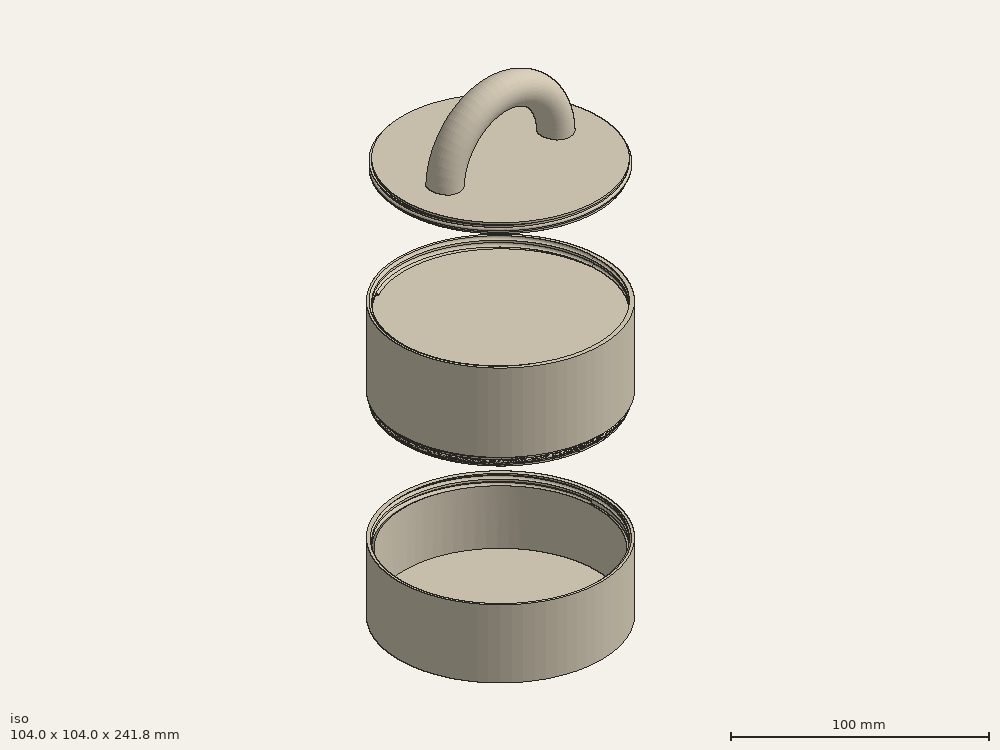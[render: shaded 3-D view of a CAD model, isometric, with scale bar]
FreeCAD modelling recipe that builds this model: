
FCSTD DOCUMENT  (FreeCAD 0.17R13522 (Git))
Label: lior_1
License: CreativeCommons Attribution-ShareAlike
LicenseURL: http://creativecommons.org/licenses/by-sa/4.0/
objects: Part::Cut×18, Part::Feature×15, Part::Cylinder×8, Part::MultiFuse×4, Sketcher::SketchObject×3, Part::Extrusion×3, Part::Sweep×2, Part::Helix×1, PartDesign::ShapeBinder×1, PartDesign::Body×1, Part::Ellipse×1, Part::FeaturePython×1, Part::MultiCommon×1, Part::Box×1
note: 60 computed .brp shape members not serialized (recipe doc carries the construction recipe); baked Part::Feature solids carry a one-line shape summary decoded from their .brp

FEATURE [Part::Cylinder] Cylinder
  Angle = 360
  AttacherType = Attacher::AttachEngine3D
  Height = 40
  Radius = 50
FEATURE [Part::Helix] Helix
  Angle = 0
  AttacherType = Attacher::AttachEngine3D
  Height = 40
  LocalCoord = 0
  Pitch = 3
  Radius = 50
  Style = 1
FEATURE [Sketcher::SketchObject] Sketch
  MapMode = 5
  Placement = pos=(0,0,0) rot=(1,0,0;1.5708rad)
  Support = -> [XZ_Plane]
  sketch-geometry (1):
    g0: Circle CenterX=50 CenterY=0 CenterZ=0 NormalX=0 NormalY=0 NormalZ=1 AngleXU=0 Radius=1
  constraints (3):
    c: PointOnObject(g0,g-1)
    c: Radius(g0) = 1
    c: DistanceX(g-1,g0) = 50
FEATURE [Part::Sweep] Sweep
  Frenet = false
  Sections = -> [Sketch]
  Solid = true
  Spine = -> Helix
  Transition = 1
FEATURE [Part::MultiFuse] Fusion  label="base_roscada_media"
  Shapes = -> [Sweep,Cylinder]
FEATURE [Part::Cylinder] Cylinder001  label="base_parte_inferior"
  Angle = 360
  AttacherType = Attacher::AttachEngine3D
  Height = 35
  Placement = pos=(0,0,-30) rot=(0,0,1;0rad)
  Radius = 52
FEATURE [Part::Feature] Fusion001  label="base_roscada_media_para_roscar_recipiente_inferior"
  shape: bbox 110.9 x 119.3 x 43.76 mm, 46 faces (baked)
FEATURE [Part::Cut] Cut
  Base = -> Cylinder001
  Tool = -> Fusion001
FEATURE [Part::Cylinder] Cylinder002  label="perforador_parte_inferior"
  Angle = 360
  AttacherType = Attacher::AttachEngine3D
  Height = 29
  Placement = pos=(0,0,-28) rot=(0,0,1;0rad)
  Radius = 49
FEATURE [Part::Cut] Cut001  label="parte_inferior_done"
  Base = -> Cut
  Placement = pos=(0,0,-66) rot=(0,0,1;0rad)
  Tool = -> Cylinder002
FEATURE [Part::Feature] Fusion002  label="base_roscada_media001"
  shape: bbox 110.9 x 119.3 x 43.76 mm, 46 faces (baked)
FEATURE [Part::Cylinder] Cylinder003  label="Cylinder001"
  Angle = 360
  AttacherType = Attacher::AttachEngine3D
  Height = 40
  Placement = pos=(0,0,5) rot=(0,0,1;0rad)
  Radius = 52
FEATURE [Part::MultiFuse] Fusion003  label="parte_media_comienzo"
  Shapes = -> [Fusion002,Cylinder003]
FEATURE [Part::Feature] Fusion004  label="base_roscada_media002"
  Placement = pos=(0,0,8) rot=(0,0,1;0rad)
  shape: bbox 110.9 x 119.3 x 43.76 mm, 46 faces (baked)
FEATURE [Part::Cut] Cut002  label="parte_media_2"
  Base = -> Fusion003
  Tool = -> Fusion004
FEATURE [Part::Cylinder] Cylinder004  label="Cylinder002"
  Angle = 360
  AttacherType = Attacher::AttachEngine3D
  Height = 10
  Placement = pos=(0,0,-10) rot=(0,0,1;0rad)
  Radius = 60
FEATURE [Part::Cut] Cut003  label="parte_media_sin_perforar"
  Base = -> Cut002
  Tool = -> Cylinder004
FEATURE [Part::Feature] Fusion005  label="tapa_rosca"
  shape: bbox 110.9 x 119.3 x 43.76 mm, 46 faces (baked)
FEATURE [Part::Cylinder] Cylinder005  label="Cylinder003"
  Angle = 360
  AttacherType = Attacher::AttachEngine3D
  Height = 40
  Placement = pos=(0,0,4) rot=(0,0,1;0rad)
  Radius = 54
FEATURE [Part::Cut] Cut004
  Base = -> Fusion005
  Tool = -> Cylinder005
FEATURE [Part::Cylinder] Cylinder006  label="Cylinder004"
  Angle = 360
  AttacherType = Attacher::AttachEngine3D
  Height = 1
  Placement = pos=(0,0,4) rot=(0,0,1;0rad)
  Radius = 50
FEATURE [Part::MultiFuse] Fusion006
  Shapes = -> [Cut004,Cylinder006]
FEATURE [PartDesign::ShapeBinder] CopyFusion006
  Placement = pos=(0,0,4) rot=(0,0,1;0rad)
FEATURE [PartDesign::Body] Body
  Group = -> [Sketch,CopyFusion006]
  Origin = -> Origin
FEATURE [Sketcher::SketchObject] Sketch001
  Placement = pos=(0,0,0) rot=(1,0,0;1.5708rad)
  sketch-geometry (1):
    g0: ArcOfCircle CenterX=0 CenterY=0 CenterZ=0 NormalX=0 NormalY=0 NormalZ=1 AngleXU=0 Radius=30.8415 StartAngle=0.00522177 EndAngle=3.12837
  constraints (1):
    c: Coincident(g0,g-1)
FEATURE [Sketcher::SketchObject] Sketch002
  Placement = pos=(0,0,5) rot=(0,0,1;0rad)
  sketch-geometry (1):
    g0: Circle CenterX=30 CenterY=0 CenterZ=0 NormalX=0 NormalY=0 NormalZ=1 AngleXU=0 Radius=7.5
  constraints (3):
    c: PointOnObject(g0,g-1)
    c: Radius(g0) = 7.5
    c: DistanceX(g-1,g0) = 30
FEATURE [Part::Sweep] Sweep001  label="manija"
  Frenet = false
  Placement = pos=(0,0,4) rot=(0,0,1;0rad)
  Sections = -> [Sketch002]
  Solid = true
  Spine = -> Sketch001
  Transition = 1
FEATURE [Part::MultiFuse] Fusion007  label="tapa_con_rosca"
  Placement = pos=(0,0,104) rot=(0,0,1;0rad)
  Shapes = -> [Fusion006,Sweep001]
FEATURE [Part::Ellipse] Ellipse
  Angle0 = 0
  Angle1 = 360
  AttacherType = Attacher::AttachEngine3D
  MajorRadius = 5
  MinorRadius = 2.5
FEATURE [Part::Extrusion] Extrude
  Base = -> Ellipse
  Dir = (0,0,1)
  DirMode = 2
  FaceMakerClass = Part::FaceMakerBullseye
  LengthFwd = 20
  LengthRev = 0
  Solid = true
  Symmetric = false
FEATURE [Part::Extrusion] Extrude001
  Base = -> Ellipse
  Dir = (0,0,1)
  DirMode = 2
  FaceMakerClass = Part::FaceMakerBullseye
  LengthFwd = 20
  LengthRev = 0
  Solid = true
  Symmetric = false
FEATURE [Part::Extrusion] Extrude002
  Base = -> Ellipse
  Dir = (0,0,1)
  DirMode = 2
  FaceMakerClass = Part::FaceMakerBullseye
  LengthFwd = 20
  LengthRev = 0
  Solid = true
  Symmetric = false
FEATURE [Part::FeaturePython] Array  # Draft array (typed FeaturePython)
  Angle = 360
  ArrayType = 0
  Axis = (0,0,1)
  Base = -> Extrude
  Center = (0,0,0)
  Fuse = false
  IntervalAxis = (0,0,0)
  IntervalX = (14,0,0)
  IntervalY = (0,9,0)
  IntervalZ = (0,0,0)
  NumberPolar = 1
  NumberX = 30
  NumberY = 30
  NumberZ = 1
FEATURE [Part::Cylinder] Cylinder007  label="Cylinder005"
  Angle = 360
  AttacherType = Attacher::AttachEngine3D
  Height = 50
  Placement = pos=(77,135,-2) rot=(0,0,1;0rad)
  Radius = 48
FEATURE [Part::MultiCommon] Common
  Placement = pos=(39,-136,0) rot=(0,0,1;0rad)
  Shapes = -> [Array,Cylinder007]
FEATURE [Part::Box] Box  label="Cube"
  AttacherType = Attacher::AttachEngine3D
  Height = 60
  Length = 10
  Placement = pos=(92,40,-5) rot=(0,0,1;0rad)
  Width = 10
FEATURE [Part::Feature] Box001  label="Cube001"
  Placement = pos=(132,40,-5) rot=(0,0,1;0rad)
  shape: bbox 10 x 10 x 60 mm, 6 faces (baked)
FEATURE [Part::Feature] Box001001  label="Cube002"
  Placement = pos=(146,30,-5) rot=(0,0,1;0rad)
  shape: bbox 10 x 10 x 60 mm, 6 faces (baked)
FEATURE [Part::Feature] Box001001001  label="Cube003"
  Placement = pos=(77,30,-5) rot=(0,0,1;0rad)
  shape: bbox 10 x 10 x 60 mm, 6 faces (baked)
FEATURE [Part::Feature] Box001001001001  label="Cube004"
  Placement = pos=(77,-43,-5) rot=(0,0,1;0rad)
  shape: bbox 10 x 10 x 60 mm, 6 faces (baked)
FEATURE [Part::Feature] Box001001001001001  label="Cube005"
  Placement = pos=(146,-43,-5) rot=(0,0,1;0rad)
  shape: bbox 10 x 10 x 60 mm, 6 faces (baked)
FEATURE [Part::Feature] Box001001001001001001  label="Cube006"
  Placement = pos=(130,-52,-5) rot=(0,0,1;0rad)
  shape: bbox 10 x 10 x 60 mm, 6 faces (baked)
FEATURE [Part::Feature] Box001001001001001001001  label="Cube007"
  Placement = pos=(91,-52,-5) rot=(0,0,1;0rad)
  shape: bbox 10 x 10 x 60 mm, 6 faces (baked)
FEATURE [Part::Feature] Box001001001001001001002  label="Cube008"
  Placement = pos=(64,13,-5) rot=(0,0,1;0rad)
  shape: bbox 10 x 10 x 60 mm, 6 faces (baked)
FEATURE [Part::Feature] Box001001001001001001002001  label="Cube009"
  Placement = pos=(64,-25,-5) rot=(0,0,1;0rad)
  shape: bbox 10 x 10 x 60 mm, 6 faces (baked)
FEATURE [Part::Feature] Box001001001001001001002001001  label="Cube010"
  Placement = pos=(159,-25,-5) rot=(0,0,1;0rad)
  shape: bbox 10 x 10 x 60 mm, 6 faces (baked)
FEATURE [Part::Feature] Box001001001001001001002001001001  label="Cube011"
  Placement = pos=(159,12,-5) rot=(0,0,1;0rad)
  shape: bbox 10 x 10 x 60 mm, 6 faces (baked)
FEATURE [Part::Cut] Cut005
  Base = -> Common
  Tool = -> Box
FEATURE [Part::Cut] Cut006
  Base = -> Cut005
  Tool = -> Box001
FEATURE [Part::Cut] Cut007
  Base = -> Cut006
  Tool = -> Box001001
FEATURE [Part::Cut] Cut008
  Base = -> Cut007
  Tool = -> Box001001001
FEATURE [Part::Cut] Cut009
  Base = -> Cut008
  Tool = -> Box001001001001
FEATURE [Part::Cut] Cut010
  Base = -> Cut009
  Tool = -> Box001001001001001
FEATURE [Part::Cut] Cut011
  Base = -> Cut010
  Tool = -> Box001001001001001001
FEATURE [Part::Cut] Cut012
  Base = -> Cut011
  Tool = -> Box001001001001001001001
FEATURE [Part::Cut] Cut013
  Base = -> Cut012
  Tool = -> Box001001001001001001002
FEATURE [Part::Cut] Cut014
  Base = -> Cut013
  Tool = -> Box001001001001001001002001
FEATURE [Part::Cut] Cut015
  Base = -> Cut014
  Tool = -> Box001001001001001001002001001
FEATURE [Part::Cut] Cut016  label="rejilla"
  Base = -> Cut015
  Placement = pos=(-116,1,-9) rot=(0,0,1;0rad)
  Tool = -> Box001001001001001001002001001001
FEATURE [Part::Cut] Cut017  label="parte_media"
  Base = -> Cut003
  Tool = -> Cut016
